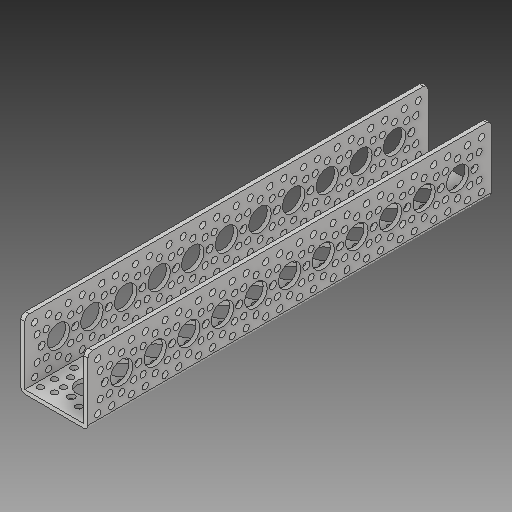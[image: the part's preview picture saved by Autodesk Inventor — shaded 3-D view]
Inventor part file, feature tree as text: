
AUTODESK INVENTOR PART (.ipt)
format: ipt  version: 2017 (Build 210142000, 142)  size: 602,112 bytes
history: native  units: in
note: dims shown in document units (in); Inventor stores cm internally (conversion verified against a paired STEP export)
features: fillet x1
ambient origin geometry x8: Origin, YZ Plane, XZ Plane, XY Plane, X Axis, Y Axis, Z Axis, Center Point
bodies: Solid1 (feature_tree)
feature tree (1):
  fillet  "Fillet1"  [1 undecoded]
note: 1 required parameter value undecoded (feature->parameter linkage not recoverable at this tier; creation-order binding heuristic only, values carry confidence <= 0.55)
